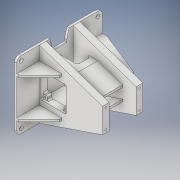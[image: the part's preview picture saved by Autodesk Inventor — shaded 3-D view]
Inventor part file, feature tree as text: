
AUTODESK INVENTOR PART (.ipt)
format: ipt  version: 2019.3 (Build 233278000, 278)  size: 455,168 bytes
history: native  units: mm
features: extrude x18, sketch x17, chamfer x7, projected_geometry x4, other x3, fillet x1, reference x1
ambient origin geometry x8: Origin, YZ Plane, XZ Plane, XY Plane, X Axis, Y Axis, Z Axis, Center Point
bodies: Solid1 (feature_tree)
feature tree (51):
  extrude  "Extrusion1"  Depth=27.5mm
  extrude  "Extrusion2"  Depth=150.0mm
  extrude  "Extrusion3"  Depth=15.0mm TaperAngle=0.0deg
  extrude  "Extrusion4"  Depth=75.0mm TaperAngle=0.0deg
  extrude  "Extrusion5"  Depth=15.0mm
  extrude  "Extrusion6"  Depth=31.75mm
  extrude  "Extrusion7"  Depth=25.0mm TaperAngle=0.0deg
  extrude  "Extrusion8"  Depth=50.0mm TaperAngle=0.0deg
  extrude  "Extrusion9"  Depth=9.0mm
  chamfer  "Chamfer3"  Distance=10.0mm
  chamfer  "Chamfer4"  Distance=10.0mm
  fillet  "Fillet1"  Radius=50.0mm
  chamfer  "Chamfer5"  Distance=110.0mm
  chamfer  "Chamfer6"  Distance=40.0mm Angle=45.0deg
  extrude  "Extrusion10"  Depth=40.0mm TaperAngle=45.0deg
  extrude  "Extrusion11"  Depth=10.0mm
  extrude  "Extrusion12"  Depth=20.0mm TaperAngle=15.0deg
  chamfer  "Chamfer7"  Distance=20.0mm Angle=15.0deg
  chamfer  "Chamfer8"  Distance=7.5mm
  extrude  "MidRibs"  Depth=7.5mm
  extrude  "MotorFaceRib"  Depth=7.5mm
  chamfer  "Chamfer9"  Distance=7.5mm
  extrude  "MotorIndent"  Depth=5.0mm
  extrude  "MotorHole"  Depth=5.0mm
  extrude  "Extrusion19"  Depth=5.0mm
  extrude  "Extrusion20"  Depth=5.0mm
  sketch  "Sketch1"  dims[d0=55.0mm d1=27.5mm]
  reference  "Reference1"
  sketch  "Sketch2"  dims[d2=14.0mm d3=150.0mm]
  projected_geometry  "Projected Loop1"
  sketch  "Sketch3"  dims[d4=140.0mm d5=15.0mm d6=0.0mm]
  projected_geometry  "Projected Loop2"
  sketch  "Sketch4"  dims[d7=5.0mm d8=0.0mm d9=75.0mm d10=0.0mm]
  projected_geometry  "Projected Loop3"
  sketch  "Sketch5"  dims[d11=15.0mm d12=15.0mm]
  sketch  "Sketch6"  dims[d13=80.0mm d14=0.0mm d15=31.75mm]
  projected_geometry  "Projected Loop4"
  sketch  "Sketch7"  dims[d16=29.125mm d17=25.0mm d18=0.0mm]
  sketch  "Sketch8"  dims[d19=50.0mm d20=0.0mm d21=50.0mm d22=0.0mm]
  sketch  "Sketch9"  dims[d23=9.0mm d24=9.0mm]
  sketch  "Sketch10"  dims[d25=9.0mm]
  sketch  "Sketch12"  dims[d26=9.0mm]
  sketch  "Sketch13"  dims[d27=10.0mm]
  sketch  "Sketch17"  dims[d28=10.0mm]
  sketch  "Sketch18"  dims[d29=10.0mm]
  sketch  "Sketch19"  dims[d30=10.0mm]
  sketch  "Sketch20"  dims[d31=10.0mm]
  sketch  "Sketch21"  dims[d32=10.0mm d33=10.0mm d34=10.0mm d35=50.0mm d36=0.0mm d40=110.0mm d41=0.0mm d48=40.0mm d49=100.0mm d50=45.0deg d51=40.0mm d52=100.0mm d53=45.0deg d54=10.0mm d55=20.0mm d56=100.0mm d57=15.0deg d58=20.0mm d59=100.0mm d60=15.0deg d61=7.5mm d62=7.5mm d63=7.5mm d64=7.5mm d65=42.5mm d66=42.5mm d67=6.25mm d68=6.25mm d69=4.0mm d70=4.0mm d71=4.0mm d72=4.0mm d73=25.0mm d74=0.0mm d77=5.0mm d82=38.1mm d92=25.0mm d93=0.0mm d110=31.75mm d111=29.125mm d112=25.0mm d113=0.0mm d114=20.0mm d115=2.0mm d116=15.0deg d117=20.0mm d118=2.0mm d119=15.0deg d120=5.0mm d122=55.0mm d123=0.0mm d142=30.0mm d143=50.0mm d144=0.0mm d145=45.0mm d146=2.0mm d147=45.0deg d153=27.5mm d154=110.0mm d157=56.5mm d158=56.5mm d159=28.25mm d160=30.0mm d161=3.0mm d162=5.0mm d163=0.0mm d164=4.0mm d165=47.0mm d166=23.5mm d167=47.0mm d168=47.0mm d169=47.0mm d173=23.5mm d176=4.5mm d177=4.5mm d178=9.25mm d179=9.25mm d180=3.0mm d181=3.0mm d182=5.0mm d183=0.0mm d184=15.0mm d185=5.0mm d186=15.0mm d187=30.0mm d189=30.0mm d193=5.0mm d194=0.0mm d195=30.0mm d196=40.0mm d197=5.0mm d198=5.0mm d199=5.0mm d200=5.0mm d201=5.0mm d202=0.0mm]
  parser-record x1  (decoder bookkeeping rows leaked as tree rows — omitted from the tree; the rows remain in map.json)
  other  "Assembly.iam"
  other  "VerticalBar:1"
note: 1 file-system path scrubbed to <path> (originals preserved in map.json)
